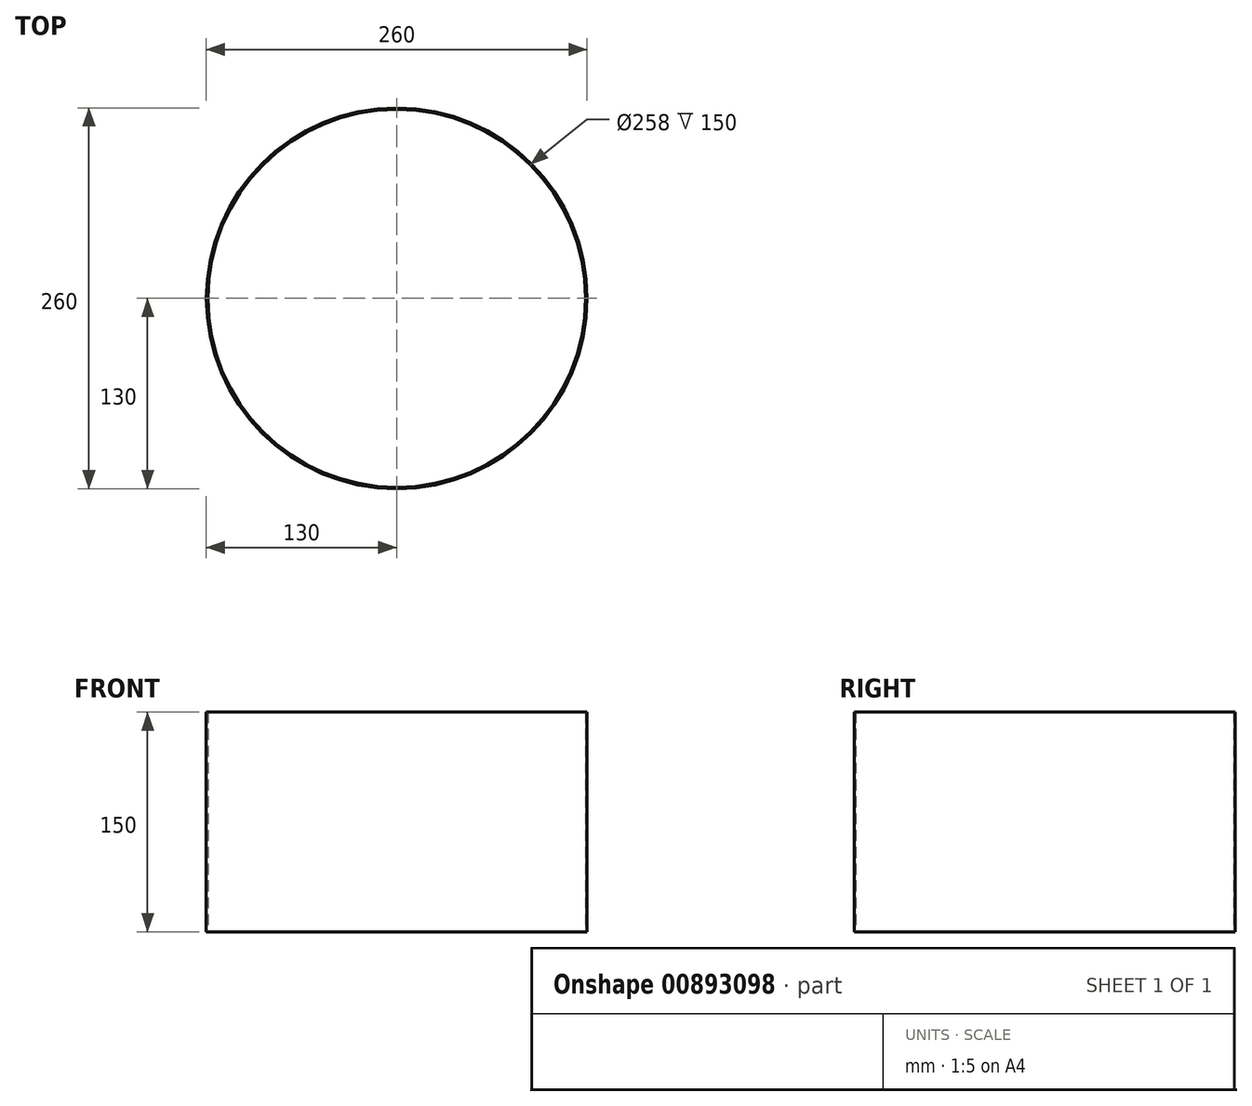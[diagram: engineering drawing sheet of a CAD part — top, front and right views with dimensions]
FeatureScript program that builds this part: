
annotation { "Feature Type Name" : "Feature", "Feature Type Description" : "" }
export const myFeature = defineFeature(function(context is Context, id is Id, definition is map)
    precondition{}
    {
        {
            var Q0;
            Q0=qCreatedBy(makeId("Top.planeOp"),FACE);
            var sketch = newSketch(context, id + "F0", { "sketchPlane" : qUnion([Q0])});
            skCircle(sketch, "E0", {"center": v(0, 0) * mm, "radius": 130 * mm});
            skCircle(sketch, "E1", {"center": v(0, 0) * mm, "radius": 129 * mm});
            skSolve(sketch);
        }
        {
            var Q0;
            Q0=makeQuery(id+"F0.imprint","IMPRINT",FACE,{"disambiguationData":[TD([[makeQuery(id+"F0.imprint","IMPRINT",EDGE,{"derivedFrom":sQuery(id+"F0.wireOp",EDGE,"E0")}),1.0]])]});
            extrude(context, id + "F1", {"entities" : qUnion([Q0]), "depth" : 150 * mm, "offsetDistance" : 25 * mm});
        }
    });
